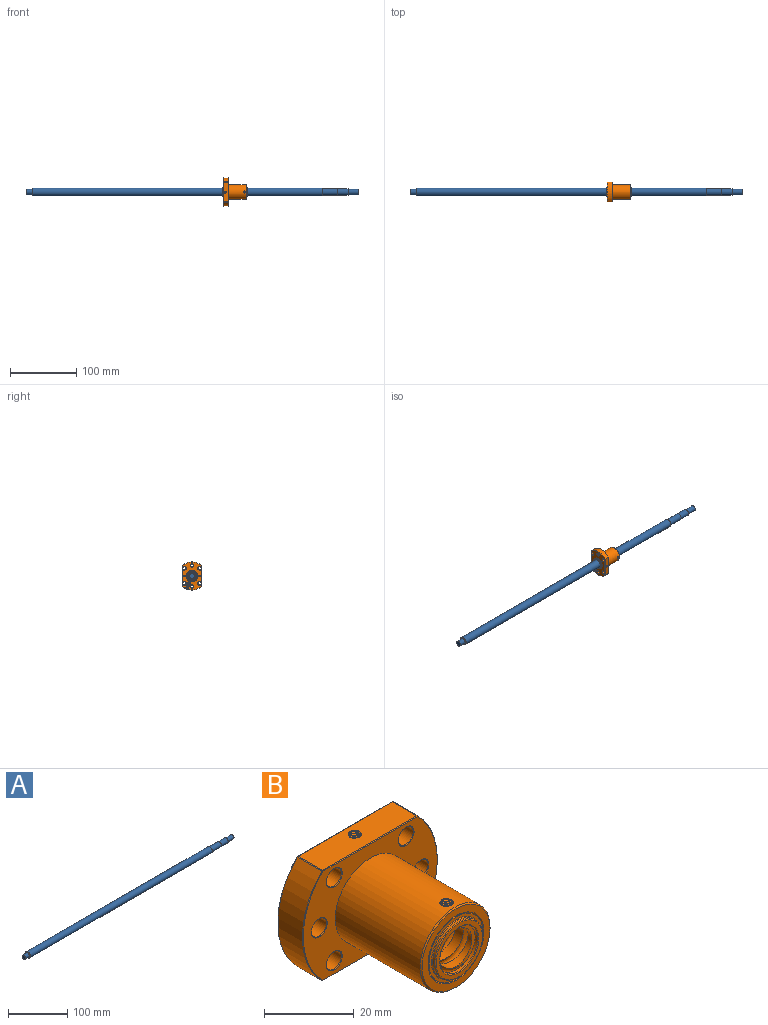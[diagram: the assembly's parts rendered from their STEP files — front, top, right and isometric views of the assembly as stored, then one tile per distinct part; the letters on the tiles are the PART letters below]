
ASSEMBLY  parts=2 mates=1
PART A: 11 faces, bbox 500x12x12 mm
  f0: cylinder r=5mm len=23mm, axis (-1,0,0), area 722.6mm2, adj f1,f10
  f1: plane 12x12mm, normal (1,0,0), area 34.6mm2, adj f0,f2
  f2: cylinder r=6mm len=436mm, axis (-1,0,0), area 16436.8mm2, adj f1,f3
  f3: plane 12x12mm, normal (-1,0,0), area 62.8mm2, adj f2,f4
  f4: cylinder r=4mm len=10mm, axis (-1,0,0), area 251.3mm2, adj f3,f5
  f5: plane 8x8mm, normal (-1,0,0), area 50.3mm2, adj f4
  f6: plane 8x8mm, normal (1,0,0), area 50.3mm2, adj f7
  f7: cylinder r=4mm len=15mm, axis (-1,0,0), area 377mm2, adj f6,f8
  f8: plane 9.9x9.9mm, normal (1,0,0), area 26.7mm2, adj f7,f9
  f9: cylinder r=4.95mm len=16mm, axis (-1,0,0), area 497.6mm2, adj f8,f10
  f10: plane 10x10mm, normal (1,0,0), area 1.6mm2, adj f0,f9
PART B: 102 faces, bbox 45.1x42.8x33 mm
  f0: cylinder r=1.54mm len=6.58mm, axis (0,0,-1), area 14.7mm2, adj f1,f3,f4,f5
  f1: bspline ~6.91x3.09mm, area 37.3mm2, adj f0,f2,f3,f5
  f2: cylinder r=1.26mm len=6.56mm, axis (0,0,-1), area 6.5mm2, adj f1,f3,f4,f5
  f3: cylinder r=8.5mm len=2.9mm, axis (0,1,0), area 6.1mm2, adj f0,f1,f2,f4
  f4: bspline ~6.88x3.09mm, area 37.4mm2, adj f0,f2,f3,f5
  f5: plane 29.89x7.84mm, normal (0,0,1), area 222.7mm2, adj f0,f1,f2,f4,f6,f99,f100,f101
  f6: cylinder r=0.3mm len=7.7mm, axis (0,1,0), area 1.8mm2, adj f5,f7,f97,f98
  f7: cylinder r=21.21mm len=29.82mm, axis (0,1,0), area 254.6mm2, adj f6,f8,f95,f96
  f8: cylinder r=0.3mm len=7.7mm, axis (0,1,0), area 1.8mm2, adj f7,f9,f93,f94
  f9: plane 29.89x7.84mm, normal (0,0,-1), area 222.7mm2, adj f8,f10,f12,f13,f14,f15,f91,f92
  f10: cylinder r=1.26mm len=6.59mm, axis (0,0,-1), area 6.5mm2, adj f9,f11,f12,f14
  f11: cylinder r=8.5mm len=2.87mm, axis (0,1,0), area 6.3mm2, adj f10,f12,f13,f14
  f12: bspline ~6.91x3.08mm, area 37.3mm2, adj f9,f10,f11,f13
  f13: cylinder r=1.54mm len=6.62mm, axis (0,0,-1), area 14.8mm2, adj f9,f11,f12,f14
  f14: bspline ~6.94x3.09mm, area 37.4mm2, adj f9,f10,f11,f13
  f15: cylinder r=0.3mm len=7.7mm, axis (0,1,0), area 1.8mm2, adj f9,f16,f89,f90
  f16: cylinder r=21.21mm len=29.82mm, axis (0,1,0), area 231mm2, adj f15,f17,f26,f88,f100
  f17: cone r=2.88mm half-angle=45deg, axis (0.92,0,0.38), area 8.5mm2, adj f16,f18,f25
  f18: plane 5.88x5.55mm, normal (-0.92,0,-0.38), area 5.3mm2, adj f17,f19,f23,f24
  f19: bspline ~12.73x9.06mm, area 141.6mm2, adj f18,f20,f24,f25
  f20: cylinder r=8.5mm len=5.73mm, axis (0,1,0), area 23.7mm2, adj f19,f21,f22,f23,f24,f25
  f21: cylinder r=3.07mm len=4.12mm, axis (-0.92,0,-0.38), area 0.4mm2, adj f20,f22,f23
  f22: plane 3.48x0.53mm, normal (0.92,0,0.38), area 1.3mm2, adj f20,f21,f23
  f23: bspline ~13.61x9.15mm, area 141.4mm2, adj f18,f20,f21,f22,f24,f25
  f24: cylinder r=3.07mm len=13.86mm, axis (-0.92,0,-0.38), area 55.7mm2, adj f18,f19,f20,f23
  f25: cylinder r=2.52mm len=13.38mm, axis (-0.92,0,-0.38), area 24.4mm2, adj f17,f19,f20,f23
  f26: cone r=21.14mm half-angle=45deg, axis (0,-1,0), area 7mm2, adj f16,f27,f28,f89
  f27: cone r=0.23mm half-angle=45deg, axis (0,-1,0), area 0mm2, adj f26,f28,f99,f100
  f28: plane 42.13x29.7mm, normal (0,1,0), area 776.8mm2, adj f26,f27,f29,f82,f83,f84,f85,f86
  f29: cone r=2.43mm half-angle=45deg, axis (0,1,0), area 3.2mm2, adj f28,f30
  f30: cylinder r=2.35mm len=7.7mm, axis (0,1,0), area 113.7mm2, adj f29,f31
  f31: cone r=2.43mm half-angle=45deg, axis (0,-1,0), area 3.2mm2, adj f30,f32
  f32: plane 42.13x29.7mm, normal (0,-1,0), area 640mm2, adj f31,f33,f35,f37,f75,f77,f79,f81
  f33: cone r=2.43mm half-angle=45deg, axis (0,-1,0), area 3.2mm2, adj f32,f34
  f34: cylinder r=2.35mm len=7.7mm, axis (0,1,0), area 113.7mm2, adj f33,f82
  f35: cone r=2.43mm half-angle=45deg, axis (0,-1,0), area 3.2mm2, adj f32,f36
  f36: cylinder r=2.35mm len=7.7mm, axis (0,1,0), area 113.7mm2, adj f35,f83
  f37: cylinder r=11mm len=26.7mm, axis (0,1,0), area 1833mm2, adj f32,f38,f40,f41,f42,f43,f47,f48
  f38: cylinder r=1.54mm len=3.09mm, axis (0,0,-1), area 5.6mm2, adj f37,f39,f40,f42
  f39: cylinder r=8.5mm len=2.87mm, axis (0,1,0), area 6.3mm2, adj f38,f40,f41,f42
  f40: bspline ~3.06x3.03mm, area 14.5mm2, adj f37,f38,f39,f41
  f41: cylinder r=1.26mm len=2.54mm, axis (0,0,-1), area 2.5mm2, adj f37,f39,f40,f42
  f42: bspline ~3.07x3.07mm, area 14.4mm2, adj f37,f38,f39,f41
  f43: cylinder r=1.54mm len=3.09mm, axis (0,0,-1), area 5.6mm2, adj f37,f44,f47,f49
  f44: cylinder r=8.5mm len=2.9mm, axis (0,1,0), area 6.4mm2, adj f43,f45,f46,f47,f48,f49
  f45: bspline ~1.42x0.44mm, area 0mm2, adj f44,f49
  f46: bspline ~1.4x0.42mm, area 0mm2, adj f44,f47
  f47: bspline ~3.04x3mm, area 14.4mm2, adj f37,f43,f44,f46,f48
  f48: cylinder r=1.26mm len=2.54mm, axis (0,0,-1), area 2.5mm2, adj f37,f44,f47,f49
  f49: bspline ~3.07x3.06mm, area 14.5mm2, adj f37,f43,f44,f45,f48
  f50: cone r=10.85mm half-angle=45deg, axis (0,1,0), area 28.9mm2, adj f37,f51
  f51: plane 21.4x21.4mm, normal (0,-1,0), area 116.4mm2, adj f50,f52
  f52: cone r=8.65mm half-angle=45deg, axis (0,-1,0), area 23.1mm2, adj f51,f53
  f53: cylinder r=8.5mm len=17mm, axis (0,1,0), area 16mm2, adj f52,f54
  f54: plane 17x17mm, normal (0,-1,0), area 40.7mm2, adj f53,f55
  f55: torus R=7.7mm, axis (0,1,0), area 14.9mm2, adj f54,f56
  f56: cylinder r=7.5mm len=15mm, axis (0,-1,0), area 28.3mm2, adj f55,f57
  f57: torus R=7.3mm, axis (0,-1,0), area 14.7mm2, adj f56,f58
  f58: plane 14.6x14.6mm, normal (0,-1,0), area 46.7mm2, adj f57,f59
  f59: torus R=6.2mm, axis (0,1,0), area 12mm2, adj f58,f60
  f60: cylinder r=6mm len=12mm, axis (0,-1,0), area 30.2mm2, adj f59,f61,f74
  f61: plane 12.71x9.53mm, normal (0,-1,0), area 15.4mm2, adj f60,f62,f73
  f62: cylinder r=5mm len=35mm, axis (0,1,0), area 687.2mm2, adj f61,f63,f73
  f63: plane 12.7x9.53mm, normal (0,1,0), area 15.8mm2, adj f62,f64,f73
  f64: cylinder r=6mm len=12mm, axis (0,1,0), area 30.2mm2, adj f63,f65,f72
  f65: torus R=6.2mm, axis (0,-1,0), area 12mm2, adj f64,f66
  f66: plane 14.6x14.6mm, normal (0,1,0), area 46.7mm2, adj f65,f67
  f67: torus R=7.3mm, axis (0,1,0), area 14.7mm2, adj f66,f68
  f68: cylinder r=7.5mm len=15mm, axis (0,1,0), area 28.3mm2, adj f67,f69
  f69: torus R=7.7mm, axis (0,-1,0), area 14.9mm2, adj f68,f70
  f70: plane 17x17mm, normal (0,1,0), area 40.7mm2, adj f69,f71
  f71: cylinder r=8.5mm len=17mm, axis (0,1,0), area 16mm2, adj f70,f84
  f72: plane 16.28x12.22mm, normal (0,-1,0), area 25.2mm2, adj f64,f73
  f73: bspline ~40.16x15.17mm, area 2170mm2, adj f61,f62,f63,f72,f74
  f74: plane 16.29x12.23mm, normal (0,1,0), area 25.4mm2, adj f60,f73
  f75: cone r=2.43mm half-angle=45deg, axis (0,-1,0), area 3.2mm2, adj f32,f76
  f76: cylinder r=2.35mm len=7.7mm, axis (0,1,0), area 113.7mm2, adj f75,f85
  f77: cone r=2.43mm half-angle=45deg, axis (0,-1,0), area 3.2mm2, adj f32,f78
  f78: cylinder r=2.35mm len=7.7mm, axis (0,1,0), area 113.7mm2, adj f77,f86
  f79: cone r=2.43mm half-angle=45deg, axis (0,-1,0), area 3.2mm2, adj f32,f80
  f80: cylinder r=2.35mm len=7.7mm, axis (0,1,0), area 113.7mm2, adj f79,f87
  f81: cone r=0.23mm half-angle=45deg, axis (0,1,0), area 0mm2, adj f32,f88,f100,f101
  f82: cone r=2.43mm half-angle=45deg, axis (0,1,0), area 3.2mm2, adj f28,f34
  f83: cone r=2.43mm half-angle=45deg, axis (0,1,0), area 3.2mm2, adj f28,f36
  f84: cone r=8.65mm half-angle=45deg, axis (0,1,0), area 23.1mm2, adj f28,f71
  f85: cone r=2.43mm half-angle=45deg, axis (0,1,0), area 3.2mm2, adj f28,f76
  f86: cone r=2.43mm half-angle=45deg, axis (0,1,0), area 3.2mm2, adj f28,f78
  f87: cone r=2.43mm half-angle=45deg, axis (0,1,0), area 3.2mm2, adj f28,f80
  f88: cone r=21.14mm half-angle=45deg, axis (0,1,0), area 7mm2, adj f16,f32,f81,f90
  f89: cone r=0.23mm half-angle=45deg, axis (0,-1,0), area 0mm2, adj f15,f26,f28,f91
  f90: cone r=0.23mm half-angle=45deg, axis (0,1,0), area 0mm2, adj f15,f32,f88,f92
  f91: plane 29.75x0.15mm, normal (0,0.71,-0.71), area 6.3mm2, adj f9,f28,f89,f93
  f92: plane 29.75x0.15mm, normal (0,-0.71,-0.71), area 6.3mm2, adj f9,f32,f90,f94
  f93: cone r=0.23mm half-angle=45deg, axis (0,-1,0), area 0mm2, adj f8,f28,f91,f95
  f94: cone r=0.23mm half-angle=45deg, axis (0,1,0), area 0mm2, adj f8,f32,f92,f96
  f95: cone r=21.14mm half-angle=45deg, axis (0,-1,0), area 7mm2, adj f7,f28,f93,f97
  f96: cone r=21.14mm half-angle=45deg, axis (0,1,0), area 7mm2, adj f7,f32,f94,f98
  f97: cone r=0.23mm half-angle=45deg, axis (0,-1,0), area 0mm2, adj f6,f28,f95,f99
  f98: cone r=0.23mm half-angle=45deg, axis (0,1,0), area 0mm2, adj f6,f32,f96,f101
  f99: plane 29.75x0.15mm, normal (0,0.71,0.71), area 6.3mm2, adj f5,f27,f28,f97
  f100: cylinder r=0.3mm len=7.7mm, axis (0,1,0), area 1.8mm2, adj f5,f16,f27,f81
  f101: plane 29.75x0.15mm, normal (0,-0.71,0.71), area 6.3mm2, adj f5,f32,f81,f98
PLACE A at identity fixed
PLACE B rot(axis=(-0.58,0.58,0.58),120deg) t=(103.9,0,0)mm
MATE slider B.f3 <-> A.f0  axis (-1,0,0) through (86.4,0,0)mm
